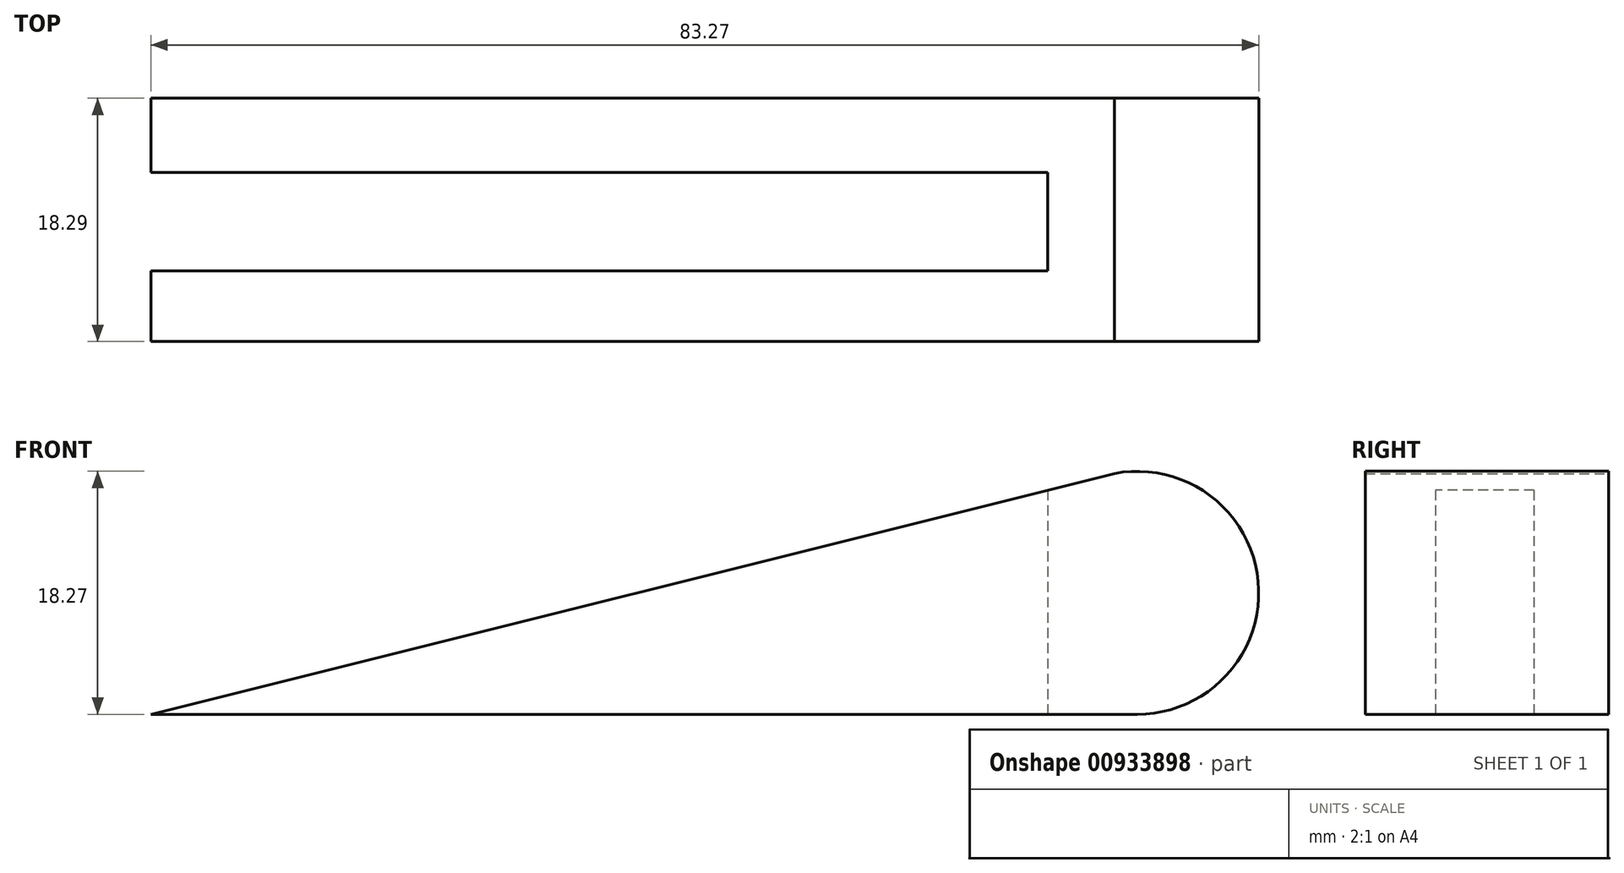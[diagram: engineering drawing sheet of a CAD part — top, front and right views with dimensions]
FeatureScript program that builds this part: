
annotation { "Feature Type Name" : "Feature", "Feature Type Description" : "" }
export const myFeature = defineFeature(function(context is Context, id is Id, definition is map)
    precondition{}
    {
        {
            var Q0;
            Q0=qCreatedBy(makeId("Front.planeOp"),FACE);
            var sketch = newSketch(context, id + "F0", { "sketchPlane" : qUnion([Q0])});
            skLineSegment(sketch, "E0", {"start": v(30.43, 18.1) * mm, "end": v(-42, 0) * mm});
            skLineSegment(sketch, "E1", {"start": v(-42, 0) * mm, "end": v(32.14, 0) * mm});
            skArc(sketch, "E2", {"start": v(32.14, 0) * mm, "mid": v(41.23, 10) * mm, "end": v(30.43, 18.1) * mm});
            skSolve(sketch);
        }
        {
            var Q0;
            Q0=makeQuery(id+"F0.imprint","IMPRINT",FACE,{"disambiguationData":[TD([[makeQuery(id+"F0.imprint","IMPRINT",EDGE,{"derivedFrom":sQuery(id+"F0.wireOp",EDGE,"E0")}),1.0]])]});
            extrude(context, id + "F1", {"entities" : qUnion([Q0]), "depth" : 18.29 * mm, "offsetDistance" : 25.4 * mm});
        }
        {
            var Q0;
            Q0=qCreatedBy(makeId("Right.planeOp"),FACE);
            var sketch = newSketch(context, id + "F2", { "sketchPlane" : qUnion([Q0])});
            skLineSegment(sketch, "E3.bottom", {"start": v(-5.6, 23.04) * mm, "end": v(-12.99, 23.04) * mm});
            skLineSegment(sketch, "E3.top", {"start": v(-5.6, -8.82) * mm, "end": v(-12.99, -8.82) * mm});
            skLineSegment(sketch, "E3.left", {"start": v(-5.6, 23.04) * mm, "end": v(-5.6, -8.82) * mm});
            skLineSegment(sketch, "E3.right", {"start": v(-12.99, 23.04) * mm, "end": v(-12.99, -8.82) * mm});
            skSolve(sketch);
        }
        {
            var Q0;
            Q0=makeQuery(id+"F2.imprint","IMPRINT",FACE,{"disambiguationData":[TD([[makeQuery(id+"F2.imprint","IMPRINT",EDGE,{"derivedFrom":sQuery(id+"F2.wireOp",EDGE,"E3.bottom")}),1.0]])]});
            extrude(context, id + "F3", {"entities" : qUnion([Q0]), "operationType" : NewBodyOperationType.REMOVE, "oppositeDirection" : true, "depth" : 54.86 * mm, "offsetDistance" : 25.4 * mm, "hasSecondDirection" : true, "secondDirectionOppositeDirection" : false, "secondDirectionDepth" : 25.4 * mm});
        }
    });
